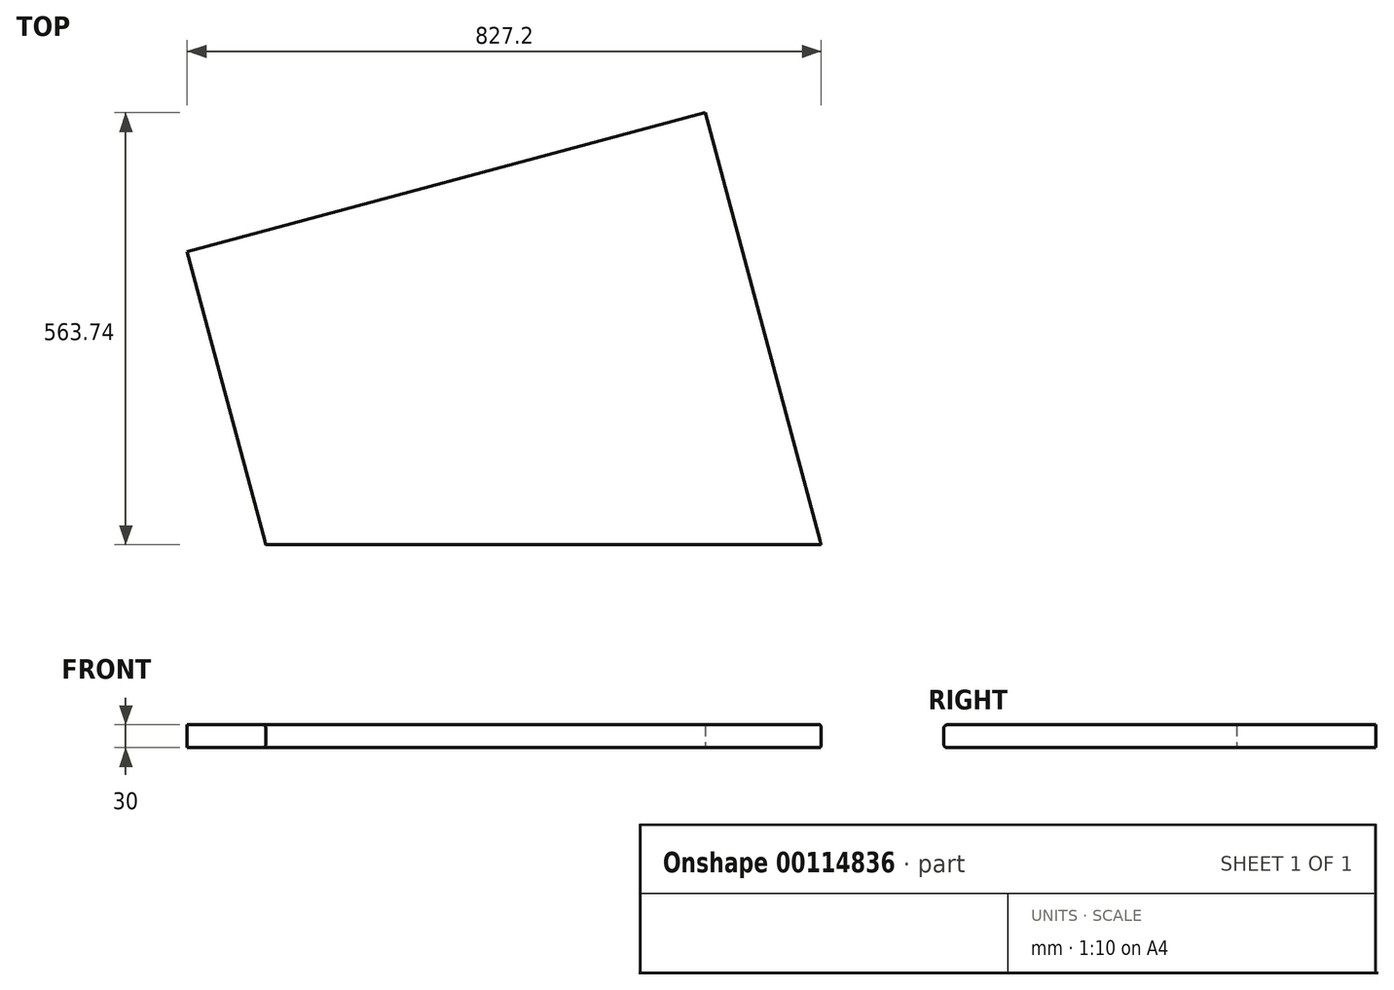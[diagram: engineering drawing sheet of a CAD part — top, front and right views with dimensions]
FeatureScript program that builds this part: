
annotation { "Feature Type Name" : "Feature", "Feature Type Description" : "" }
export const myFeature = defineFeature(function(context is Context, id is Id, definition is map)
    precondition{}
    {
        {
            var Q0;
            Q0=qCreatedBy(makeId("Right.planeOp"),FACE);
            var sketch = newSketch(context, id + "F0", { "sketchPlane" : qUnion([Q0])});
            skLineSegment(sketch, "E0.bottom", {"start": v(325, 15) * mm, "end": v(-320, 15) * mm});
            skLineSegment(sketch, "E0.top", {"start": v(325, -15) * mm, "end": v(-320, -15) * mm});
            skLineSegment(sketch, "E0.left", {"start": v(325, 15) * mm, "end": v(325, -15) * mm});
            skLineSegment(sketch, "E0.right", {"start": v(-325, 10) * mm, "end": v(-325, -10) * mm});
            skPoint(sketch, "E0.middle", {"position": v(0, 0) * mm});
            skPoint(sketch, "E1.visualSharp", {"position": v(-325, 15) * mm});
            skArc(sketch, "E1.filletArc", {"start": v(-320, 15) * mm, "mid": v(-323.54, 13.54) * mm, "end": v(-325, 10) * mm});
            skPoint(sketch, "E2.visualSharp", {"position": v(-325, -15) * mm});
            skArc(sketch, "E2.filletArc", {"start": v(-325, -10) * mm, "mid": v(-323.54, -13.54) * mm, "end": v(-320, -15) * mm});
            skSolve(sketch);
        }
        {
            var Q0;
            Q0=qCreatedBy(makeId("Top.planeOp"),FACE);
            var sketch = newSketch(context, id + "F1", { "sketchPlane" : qUnion([Q0])});
            skLineSegment(sketch, "E3.bottom", {"start": v(450, 325) * mm, "end": v(-450, 325) * mm, "construction": true});
            skLineSegment(sketch, "E3.top", {"start": v(450, -325) * mm, "end": v(-450, -325) * mm, "construction": true});
            skLineSegment(sketch, "E3.left", {"start": v(450, 325) * mm, "end": v(450, -325) * mm, "construction": true});
            skLineSegment(sketch, "E3.right", {"start": v(-450, 325) * mm, "end": v(-450, -325) * mm, "construction": true});
            skPoint(sketch, "E3.middle", {"position": v(0, 0) * mm});
            skLineSegment(sketch, "E4", {"start": v(0, 0) * mm, "end": v(450, 0) * mm, "construction": true});
            skLineSegment(sketch, "E5", {"start": v(450, 0) * mm, "end": v(450, 120.58) * mm, "construction": true});
            skLineSegment(sketch, "E6", {"start": v(450, 120.58) * mm, "end": v(0, 0) * mm, "construction": true});
            skLineSegment(sketch, "E7", {"start": v(0, 0) * mm, "end": v(-450, -120.58) * mm, "construction": true});
            skLineSegment(sketch, "E8", {"start": v(-450, -295) * mm, "end": v(450, -295) * mm, "construction": true});
            skLineSegment(sketch, "E9", {"start": v(450, -325) * mm, "end": v(275.83, 325) * mm, "construction": true});
            skLineSegment(sketch, "E10", {"start": v(-274.7, -325) * mm, "end": v(-450, 329.26) * mm, "construction": true});
            skPoint(sketch, "E11", {"position": v(-337.54, -90.44) * mm});
            skPoint(sketch, "E12", {"position": v(338.6, 90.73) * mm});
            skPoint(sketch, "E13", {"position": v(-282.73, -295) * mm});
            skLineSegment(sketch, "E14", {"start": v(-282.73, -295) * mm, "end": v(393.42, -113.83) * mm, "construction": true});
            skLineSegment(sketch, "E15", {"start": v(-377.2, 57.56) * mm, "end": v(298.95, 238.74) * mm, "construction": true});
            skPoint(sketch, "E16", {"position": v(441.96, -295) * mm});
            skLineSegment(sketch, "E17", {"start": v(-274.7, -325) * mm, "end": v(-222.6, -519.42) * mm, "construction": true});
            skLineSegment(sketch, "E18", {"start": v(450, -325) * mm, "end": v(453.55, -338.25) * mm, "construction": true});
            skLineSegment(sketch, "E19", {"start": v(-222.6, -519.42) * mm, "end": v(453.55, -338.25) * mm, "construction": true});
            skLineSegment(sketch, "E20", {"start": v(-222.6, -519.42) * mm, "end": v(-377.2, 57.56) * mm});
            skLineSegment(sketch, "E21", {"start": v(-377.2, 57.56) * mm, "end": v(298.95, 238.74) * mm});
            skLineSegment(sketch, "E22", {"start": v(298.95, 238.74) * mm, "end": v(453.55, -338.25) * mm});
            skLineSegment(sketch, "E23", {"start": v(453.55, -338.25) * mm, "end": v(-222.6, -519.42) * mm});
            skSolve(sketch);
        }
        {
            var Q0;
            Q0=makeQuery(id+"F0.imprint","IMPRINT",FACE,{"disambiguationData":[TD([[makeQuery(id+"F0.imprint","IMPRINT",EDGE,{"derivedFrom":sQuery(id+"F0.wireOp",EDGE,"E0.bottom")}),1.0]])]});
            extrude(context, id + "F2", {"entities" : qUnion([Q0]), "depth" : 1000 * mm, "symmetric" : true});
        }
        {
            var Q0;
            Q0=makeQuery(id+"F1.imprint","IMPRINT",FACE,{"disambiguationData":[TD([[makeQuery(id+"F1.imprint","IMPRINT",EDGE,{"derivedFrom":sQuery(id+"F1.wireOp",EDGE,"E20")}),-1.0]])]});
            extrude(context, id + "F3", {"entities" : qUnion([Q0]), "operationType" : NewBodyOperationType.INTERSECT, "depth" : 100 * mm, "symmetric" : true});
        }
    });
